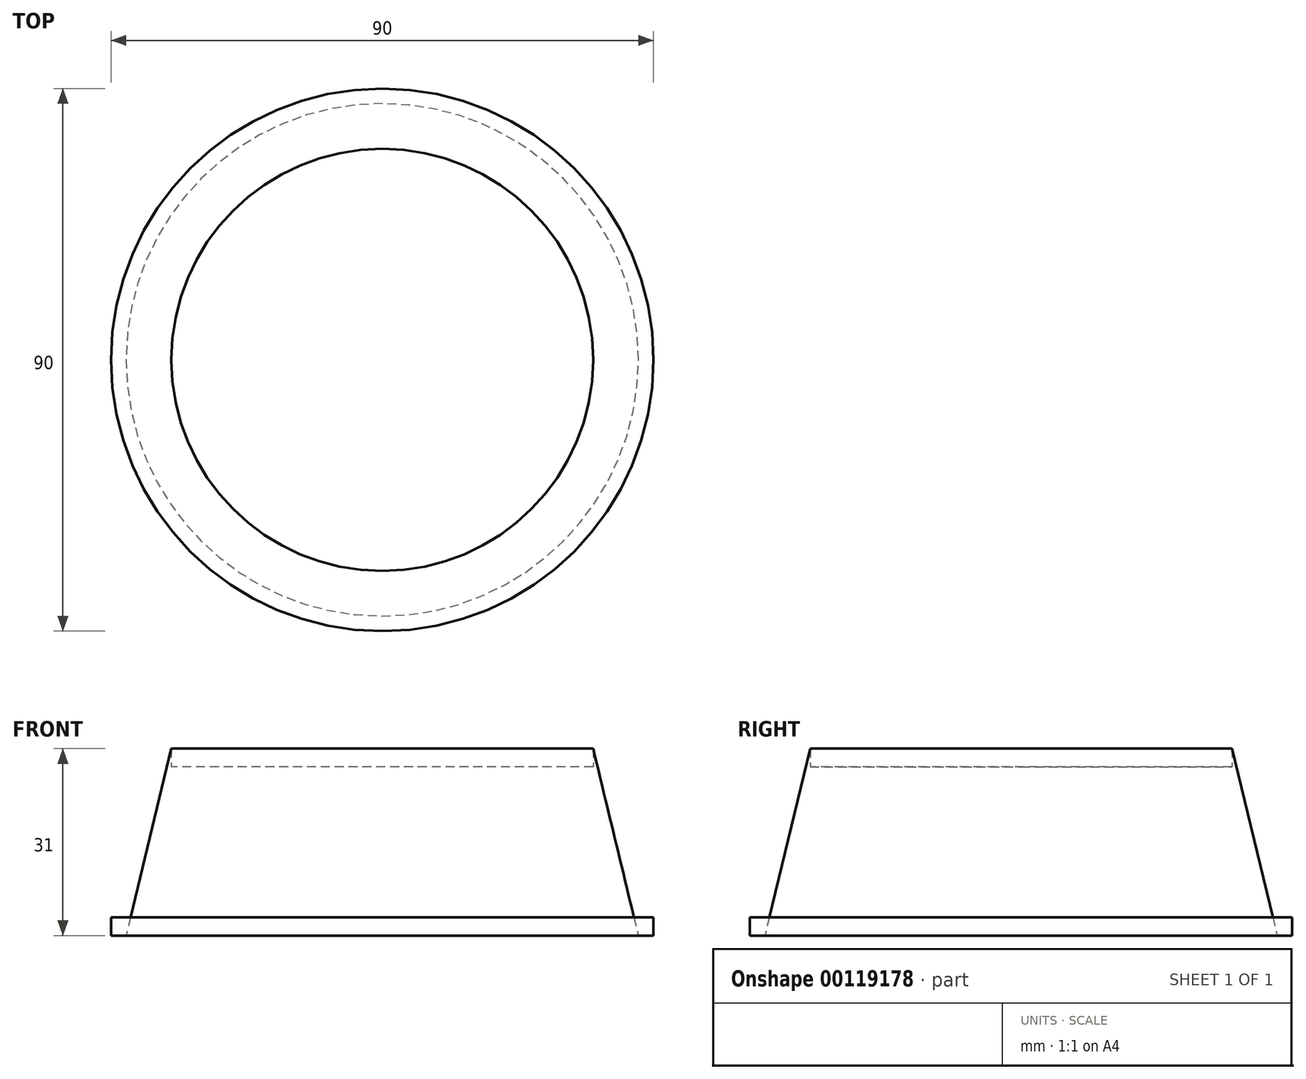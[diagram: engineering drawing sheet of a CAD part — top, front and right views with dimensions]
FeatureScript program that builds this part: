
annotation { "Feature Type Name" : "Feature", "Feature Type Description" : "" }
export const myFeature = defineFeature(function(context is Context, id is Id, definition is map)
    precondition{}
    {
        {
            var Q0;
            Q0=qCreatedBy(makeId("Top.planeOp"),FACE);
            var sketch = newSketch(context, id + "F0", { "sketchPlane" : qUnion([Q0])});
            skCircle(sketch, "E0", {"center": v(0, 0) * mm, "radius": 45 * mm});
            skCircle(sketch, "E1", {"center": v(0, 0) * mm, "radius": 42.5 * mm});
            skSolve(sketch);
        }
        {
            var Q0;
            Q0 = qSketchRegion(id + "F0", true);
            var Q1;
            Q1=makeQuery(id+"F0.imprint","IMPRINT",FACE,{"disambiguationData":[TD([[makeQuery(id+"F0.imprint","IMPRINT",EDGE,{"derivedFrom":sQuery(id+"F0.wireOp",EDGE,"E1")}),1.0]])]});
            extrude(context, id + "F1", {"entities" : qUnion([Q0, Q1]), "depth" : 3 * mm});
        }
        {
            var Q0;
            Q0=makeQuery(id+"F1.opExtrude","CAP_FACE",FACE,{"disambiguationData":[OSD([sQuery(id+"F0.wireOp",EDGE,"E0"),sQuery(id+"F0.wireOp",EDGE,"E1")])],"isStart":false});
            cPlane(context, id + "F2", {"entities" : qUnion([Q0]), "cplaneType" : CPlaneType.OFFSET, "offset" : 25 * mm, "width" : 150 * mm, "height" : 150 * mm});
        }
        {
            var Q0;
            Q0=qCreatedBy(id+"F2.planeOp",FACE);
            var sketch = newSketch(context, id + "F3", { "sketchPlane" : qUnion([Q0])});
            skCircle(sketch, "E2", {"center": v(0, 0) * mm, "radius": 35 * mm});
            skSolve(sketch);
        }
        {
            var Q0;
            Q0=makeQuery(id+"F3.imprint","IMPRINT",FACE,{"disambiguationData":[TD([[makeQuery(id+"F3.imprint","IMPRINT",EDGE,{"derivedFrom":sQuery(id+"F3.wireOp",EDGE,"E2")}),1.0]])]});
            extrude(context, id + "F4", {"entities" : qUnion([Q0]), "depth" : 3 * mm});
        }
        {
            var Q0;
            Q0=makeQuery(id+"F4.opExtrude","CAP_FACE",FACE,{"disambiguationData":[OSD([sQuery(id+"F3.wireOp",EDGE,"E2")])],"isStart":false});
            var Q1;
            Q1=makeQuery(id+"F0.imprint","IMPRINT",FACE,{"disambiguationData":[TD([[makeQuery(id+"F0.imprint","IMPRINT",EDGE,{"derivedFrom":sQuery(id+"F0.wireOp",EDGE,"E1")}),1.0]])]});
            loft(context, id + "F5", {"sheetProfilesArray" : [{ "sheetProfileEntities" : qUnion([Q0]) }, { "sheetProfileEntities" : qUnion([Q1]) }]});
        }
    });
